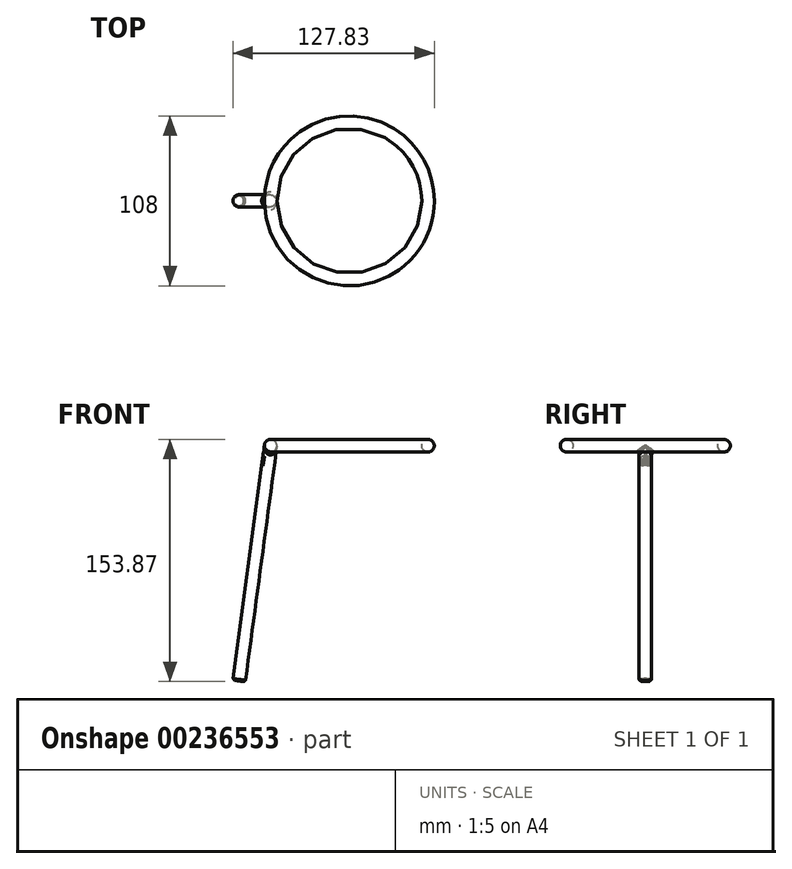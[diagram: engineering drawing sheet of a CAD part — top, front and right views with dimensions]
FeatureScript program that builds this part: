
annotation { "Feature Type Name" : "Feature", "Feature Type Description" : "" }
export const myFeature = defineFeature(function(context is Context, id is Id, definition is map)
    precondition{}
    {
        {
            var Q0;
            Q0=qCreatedBy(makeId("Front.planeOp"),FACE);
            var sketch = newSketch(context, id + "F0", { "sketchPlane" : qUnion([Q0])});
            skLineSegment(sketch, "E0", {"start": v(0, 0) * mm, "end": v(0, 178.1) * mm, "construction": true});
            skCircle(sketch, "E1", {"center": v(-50, 150) * mm, "radius": 4 * mm});
            skLineSegment(sketch, "E2.top", {"start": v(-70, 0.53) * mm, "end": v(-66.04, 0) * mm});
            skLineSegment(sketch, "E2.left", {"start": v(-50, 150) * mm, "end": v(-70, 0.53) * mm});
            skLineSegment(sketch, "E2.right", {"start": v(-46.04, 149.47) * mm, "end": v(-66.04, 0) * mm});
            skLineSegment(sketch, "E3", {"start": v(-50, 150) * mm, "end": v(-46.04, 149.47) * mm});
            skSolve(sketch);
        }
        {
            var Q0;
            {var subQ0=sQuery(id+"F0.wireOp",EDGE,"E3");Q0=makeQuery(id+"F0.imprint","IMPRINT",FACE,{"disambiguationData":[TD([[makeQuery(id+"F0.imprint","IMPRINT",EDGE,{"derivedFrom":subQ0}),1.0]])]});}
            var Q1;
            {var subQ0=sQuery(id+"F0.wireOp",EDGE,"E3");Q1=makeQuery(id+"F0.imprint","IMPRINT",FACE,{"disambiguationData":[TD([[makeQuery(id+"F0.imprint","IMPRINT",EDGE,{"derivedFrom":subQ0}),-1.0]])]});}
            var Q2;
            Q2=sQuery(id+"F0.wireOp",EDGE,"E0");
            revolve(context, id + "F1", {"entities" : qUnion([Q0, Q1]), "axis" : qUnion([Q2]), "revolveType" : RevolveType.FULL});
        }
        {
            var Q0;
            {var subQ4=sQuery(id+"F0.wireOp",EDGE,"E2.top");Q0=makeQuery(id+"F0.imprint","IMPRINT",FACE,{"disambiguationData":[TD([[makeQuery(id+"F0.imprint","IMPRINT",EDGE,{"derivedFrom":subQ4}),1.0]])]});}
            var Q1;
            {var subQ0=sQuery(id+"F0.wireOp",EDGE,"E3");Q1=makeQuery(id+"F0.imprint","IMPRINT",FACE,{"disambiguationData":[TD([[makeQuery(id+"F0.imprint","IMPRINT",EDGE,{"derivedFrom":subQ0}),-1.0]])]});}
            var Q2;
            Q2=sQuery(id+"F0.wireOp",EDGE,"E2.left");
            revolve(context, id + "F2", {"operationType" : NewBodyOperationType.ADD, "entities" : qUnion([Q0, Q1]), "axis" : qUnion([Q2]), "revolveType" : RevolveType.FULL});
        }
        {
            var Q0;
            Q0=makeQuery(id+"FIkdkUBWeoXywMX_1.1.F2.boolean.opBoolean","INTERSECT",EDGE,{"disambiguationData":[OD(1.0)],"derivedFrom":[makeQuery(id+"F1.opRevolve","SWEPT_FACE",FACE,{"disambiguationData":[OSD([sQuery(id+"F0.wireOp",EDGE,"E1")])]}),makeQuery(id+"FIkdkUBWeoXywMX_1.1.F2.opRevolve","SWEPT_FACE",FACE,{"disambiguationData":[OSD([sQuery(id+"F0.wireOp",EDGE,"E2.right")])]})]});
            var Q1;
            Q1=makeQuery(id+"FIkdkUBWeoXywMX_1.1.F2.boolean.opBoolean","INTERSECT",EDGE,{"disambiguationData":[OD(0.0)],"derivedFrom":[makeQuery(id+"F1.opRevolve","SWEPT_FACE",FACE,{"disambiguationData":[OSD([sQuery(id+"F0.wireOp",EDGE,"E1")])]}),makeQuery(id+"FIkdkUBWeoXywMX_1.1.F2.opRevolve","SWEPT_FACE",FACE,{"disambiguationData":[OSD([sQuery(id+"F0.wireOp",EDGE,"E2.right")])]})]});
            var Q2;
            Q2=makeQuery(id+"FIkdkUBWeoXywMX_1.2.F2.boolean.opBoolean","INTERSECT",EDGE,{"disambiguationData":[OD(1.0)],"derivedFrom":[makeQuery(id+"F1.opRevolve","SWEPT_FACE",FACE,{"disambiguationData":[OSD([sQuery(id+"F0.wireOp",EDGE,"E1")])]}),makeQuery(id+"FIkdkUBWeoXywMX_1.2.F2.opRevolve","SWEPT_FACE",FACE,{"disambiguationData":[OSD([sQuery(id+"F0.wireOp",EDGE,"E2.right")])]})]});
            var Q3;
            Q3=makeQuery(id+"FIkdkUBWeoXywMX_1.2.F2.boolean.opBoolean","INTERSECT",EDGE,{"disambiguationData":[OD(0.0)],"derivedFrom":[makeQuery(id+"F1.opRevolve","SWEPT_FACE",FACE,{"disambiguationData":[OSD([sQuery(id+"F0.wireOp",EDGE,"E1")])]}),makeQuery(id+"FIkdkUBWeoXywMX_1.2.F2.opRevolve","SWEPT_FACE",FACE,{"disambiguationData":[OSD([sQuery(id+"F0.wireOp",EDGE,"E2.right")])]})]});
            var Q4;
            Q4=makeQuery(id+"F2.boolean.opBoolean","INTERSECT",EDGE,{"disambiguationData":[OD(0.0)],"derivedFrom":[makeQuery(id+"F1.opRevolve","SWEPT_FACE",FACE,{"disambiguationData":[OSD([sQuery(id+"F0.wireOp",EDGE,"E1")])]}),makeQuery(id+"F2.opRevolve","SWEPT_FACE",FACE,{"disambiguationData":[OSD([sQuery(id+"F0.wireOp",EDGE,"E2.right")])]})]});
            var Q5;
            Q5=makeQuery(id+"F2.boolean.opBoolean","INTERSECT",EDGE,{"disambiguationData":[OD(1.0)],"derivedFrom":[makeQuery(id+"F1.opRevolve","SWEPT_FACE",FACE,{"disambiguationData":[OSD([sQuery(id+"F0.wireOp",EDGE,"E1")])]}),makeQuery(id+"F2.opRevolve","SWEPT_FACE",FACE,{"disambiguationData":[OSD([sQuery(id+"F0.wireOp",EDGE,"E2.right")])]})]});
            fillet(context, id + "F3", {"entities" : qUnion([Q0, Q1, Q2, Q3, Q4, Q5]), "radius" : 2 * mm, "tangentPropagation" : true, "allowEdgeOverflow" : false});
        }
        {
            var Q0;
            Q0=makeQuery(id+"F2.opRevolve","SWEPT_EDGE",EDGE,{"disambiguationData":[OSD([sQuery(id+"F0.wireOp",EDGE,"E2.top"),sQuery(id+"F0.wireOp",EDGE,"E2.right")])]});
            var Q1;
            Q1=makeQuery(id+"FIkdkUBWeoXywMX_1.1.F2.opRevolve","SWEPT_FACE",FACE,{"disambiguationData":[OSD([sQuery(id+"F0.wireOp",EDGE,"E2.top")])]});
            var Q2;
            Q2=makeQuery(id+"FIkdkUBWeoXywMX_1.2.F2.opRevolve","SWEPT_FACE",FACE,{"disambiguationData":[OSD([sQuery(id+"F0.wireOp",EDGE,"E2.top")])]});
            chamfer(context, id + "F4", {"entities" : qUnion([Q0, Q1, Q2]), "width" : 1 * mm, "tangentPropagation" : true});
        }
        {
            var Q0;
            Q0=sQuery(id+"F0.wireOp",EDGE,"E2.left");
            var Q1;
            Q1=qCreatedBy(makeId("Right.planeOp"),FACE);
            cPlane(context, id + "F5", {"entities" : qUnion([Q0, Q1]), "cplaneType" : CPlaneType.LINE_ANGLE, "offset" : 25 * mm, "angle" : 0 * degree, "width" : 150 * mm, "height" : 150 * mm});
        }
        {
            var Q0;
            Q0=qCreatedBy(id+"F5.planeOp",FACE);
            var sketch = newSketch(context, id + "F6", { "sketchPlane" : qUnion([Q0])});
            skLineSegment(sketch, "E4.bottom", {"start": v(-2.6, 128.7) * mm, "end": v(2.6, 128.7) * mm});
            skLineSegment(sketch, "E4.top", {"start": v(-2.6, 134.7) * mm, "end": v(-0.9, 134.7) * mm});
            skLineSegment(sketch, "E4.left", {"start": v(-2.6, 128.7) * mm, "end": v(-2.6, 134.7) * mm});
            skLineSegment(sketch, "E4.right", {"start": v(2.6, 128.7) * mm, "end": v(2.6, 134.7) * mm});
            skLineSegment(sketch, "E5", {"start": v(0, 134.7) * mm, "end": v(0, 128.89) * mm, "construction": true});
            skLineSegment(sketch, "E6", {"start": v(-2.6, 131.5) * mm, "end": v(2.6, 131.5) * mm, "construction": true});
            skCircle(sketch, "E7", {"center": v(0, 131.5) * mm, "radius": 1.68 * mm});
            skCircle(sketch, "E8", {"center": v(0, 131.5) * mm, "radius": 1.86 * mm});
            skArc(sketch, "E9", {"start": v(-0.9, 133.33) * mm, "mid": v(0, 129.46) * mm, "end": v(0.9, 133.33) * mm});
            skLineSegment(sketch, "E10.bottom", {"start": v(-2.43, 128.89) * mm, "end": v(2.43, 128.89) * mm});
            skLineSegment(sketch, "E10.top", {"start": v(-2.43, 134.53) * mm, "end": v(-0.9, 134.53) * mm});
            skLineSegment(sketch, "E10.left", {"start": v(-2.43, 128.89) * mm, "end": v(-2.43, 134.53) * mm});
            skLineSegment(sketch, "E10.right", {"start": v(2.43, 128.89) * mm, "end": v(2.43, 134.53) * mm});
            skCircle(sketch, "E11", {"center": v(0, 131.5) * mm, "radius": 1.5 * mm});
            skText(sketch, "E12", { "text": "PS", "fontName": "OpenSans-Bold.ttf"});
            skLineSegment(sketch, "E13", {"start": v(-0.9, 134.53) * mm, "end": v(-0.9, 133.33) * mm});
            skLineSegment(sketch, "E14", {"start": v(-0.72, 134.53) * mm, "end": v(-0.72, 133.4) * mm});
            skLineSegment(sketch, "E15", {"start": v(0.72, 134.53) * mm, "end": v(0.72, 133.4) * mm});
            skLineSegment(sketch, "E16", {"start": v(0.9, 134.53) * mm, "end": v(0.9, 133.33) * mm});
            skArc(sketch, "E17.trimOffspring", {"start": v(0.72, 133.4) * mm, "mid": v(0, 133.54) * mm, "end": v(-0.72, 133.4) * mm});
            skLineSegment(sketch, "E18.trimOffspring", {"start": v(-0.72, 134.53) * mm, "end": v(0.72, 134.53) * mm});
            skLineSegment(sketch, "E19.trimOffspring", {"start": v(0.9, 134.53) * mm, "end": v(2.43, 134.53) * mm});
            skLineSegment(sketch, "E20.trimOffspring", {"start": v(-0.72, 134.7) * mm, "end": v(0.72, 134.7) * mm});
            skLineSegment(sketch, "E21.trimOffspring", {"start": v(0.9, 134.7) * mm, "end": v(2.6, 134.7) * mm});
            skFitSpline(sketch, "E22", {"points": [v(0.9, 134.7) * mm, v(0.45, 135.64) * mm, v(0.18, 136.99) * mm], "startDerivative": vector(0.19, 3.49) * mm, "endDerivative": vector(1.34, 3.2) * mm});
            skFitSpline(sketch, "E23", {"points": [v(-0.9, 134.7) * mm, v(-0.78, 135.64) * mm, v(0.18, 136.99) * mm], "startDerivative": vector(1.88, 3.14) * mm, "endDerivative": vector(4.1, 2.05) * mm});
            skFitSpline(sketch, "E24", {"points": [v(-0.72, 134.7) * mm, v(-0.6, 135.64) * mm, v(-0.04, 136.63) * mm], "startDerivative": vector(1.7, 2.84) * mm, "endDerivative": vector(2.15, 1.2) * mm});
            skFitSpline(sketch, "E25", {"points": [v(0.72, 134.7) * mm, v(0.2, 135.64) * mm, v(-0.04, 136.63) * mm], "startDerivative": vector(0.17, 3.2) * mm, "endDerivative": vector(0.45, 1.64) * mm});
            const initialGuessF6  = {"E12": [-0.0012, 0.13075, 1, 0, 0.00144]};
            skSetInitialGuess(sketch, initialGuessF6);
            skSolve(sketch);
        }
        {
            var Q0;
            Q0=makeQuery(id+"F6.imprint","IMPRINT",FACE,{"disambiguationData":[TD([[makeQuery(id+"F6.imprint","IMPRINT",EDGE,{"derivedFrom":sQuery(id+"F6.wireOp",EDGE,"E4.bottom")}),1.0]])]});
            var Q1;
            Q1=makeQuery(id+"F6.imprint","IMPRINT",FACE,{"disambiguationData":[TD([[makeQuery(id+"F6.imprint","IMPRINT",EDGE,{"derivedFrom":sQuery(id+"F6.wireOp",EDGE,"E7")}),1.0]])]});
            var Q2;
            Q2=makeQuery(id+"F6.imprint","IMPRINT",FACE,{"disambiguationData":[TD([[makeQuery(id+"F6.imprint","IMPRINT",EDGE,{"derivedFrom":sQuery(id+"F6.wireOp",EDGE,"E12.sketch_text.stroke-0")}),-1.0]])]});
            var Q3;
            Q3=makeQuery(id+"F6.imprint","IMPRINT",FACE,{"disambiguationData":[TD([[makeQuery(id+"F6.imprint","IMPRINT",EDGE,{"derivedFrom":sQuery(id+"F6.wireOp",EDGE,"E12.sketch_text.stroke-16")}),-1.0]])]});
            extrude(context, id + "F7", {"entities" : qUnion([Q0, Q1, Q2, Q3]), "operationType" : NewBodyOperationType.ADD, "depth" : 4 * mm});
        }
        {
            var Q0;
            Q0=makeQuery(id+"F7.opExtrude","SWEPT_FACE",FACE,{"disambiguationData":[OSD([sQuery(id+"F6.wireOp",EDGE,"E20.trimOffspring")])]});
            var sketch = newSketch(context, id + "F8", { "sketchPlane" : qUnion([Q0])});
            skArc(sketch, "E26", {"start": v(-71.4, 3.5) * mm, "mid": v(-73.46, 0) * mm, "end": v(-71.4, -3.5) * mm});
            skLineSegment(sketch, "E27", {"start": v(-71.4, 3.5) * mm, "end": v(-74.45, 3.5) * mm});
            skLineSegment(sketch, "E28", {"start": v(-74.45, 3.5) * mm, "end": v(-74.45, -3.5) * mm});
            skLineSegment(sketch, "E29", {"start": v(-74.45, -3.5) * mm, "end": v(-71.4, -3.5) * mm});
            skSolve(sketch);
        }
        {
            var Q0;
            {var subQ0=sQuery(id+"F8.wireOp",EDGE,"E27");Q0=makeQuery(id+"F8.imprint","IMPRINT",FACE,{"disambiguationData":[TD([[makeQuery(id+"F8.imprint","IMPRINT",EDGE,{"derivedFrom":subQ0}),1.0]])]});}
            var Q1;
            {var subQ0=sQuery(id+"F8.wireOp",EDGE,"E26");var subQ1=sQuery(id+"F6.wireOp",EDGE,"E20.trimOffspring");var subQ4=makeQuery(id+"F7.opExtrude","CAP_EDGE",EDGE,{"disambiguationData":[OSD([subQ1])],"isStart":false});var subQ5=makeQuery(id+"F8.imprint","INTERSECT",VERTEX,{"derivedFrom":[subQ4,subQ0]});Q1=makeQuery(id+"F8.imprint","IMPRINT",FACE,{"disambiguationData":[TD([[makeQuery(id+"F8.imprint","IMPRINT",EDGE,{"disambiguationData":[TD([[subQ5,-1.0]])],"derivedFrom":subQ0}),-1.0]])]});}
            var Q2;
            {var subQ0=sQuery(id+"F8.wireOp",EDGE,"E26");var subQ1=sQuery(id+"F6.wireOp",EDGE,"E20.trimOffspring");var subQ4=makeQuery(id+"F7.opExtrude","CAP_EDGE",EDGE,{"disambiguationData":[OSD([subQ1])],"isStart":false});var subQ5=makeQuery(id+"F8.imprint","INTERSECT",VERTEX,{"derivedFrom":[subQ4,subQ0]});Q2=makeQuery(id+"F8.imprint","IMPRINT",FACE,{"disambiguationData":[TD([[makeQuery(id+"F8.imprint","IMPRINT",EDGE,{"disambiguationData":[TD([[subQ5,1.0]])],"derivedFrom":subQ0}),-1.0]])]});}
            var Q3;
            Q3=makeQuery(id+"F7.opExtrude","CAP_VERTEX",VERTEX,{"disambiguationData":[OSD([sQuery(id+"F6.wireOp",EDGE,"E22"),sQuery(id+"F6.wireOp",EDGE,"E23")])],"isStart":false});
            extrude(context, id + "F9", {"entities" : qUnion([Q0, Q1, Q2]), "operationType" : NewBodyOperationType.REMOVE, "endBound" : BoundingType.THROUGH_ALL, "oppositeDirection" : true, "depth" : 25 * mm, "hasSecondDirection" : true, "secondDirectionBound" : SecondDirectionBoundingType.UP_TO_VERTEX, "secondDirectionOppositeDirection" : false, "secondDirectionBoundEntityVertex" : qUnion([Q3]), "secondDirectionDepth" : 25 * mm});
        }
    });
